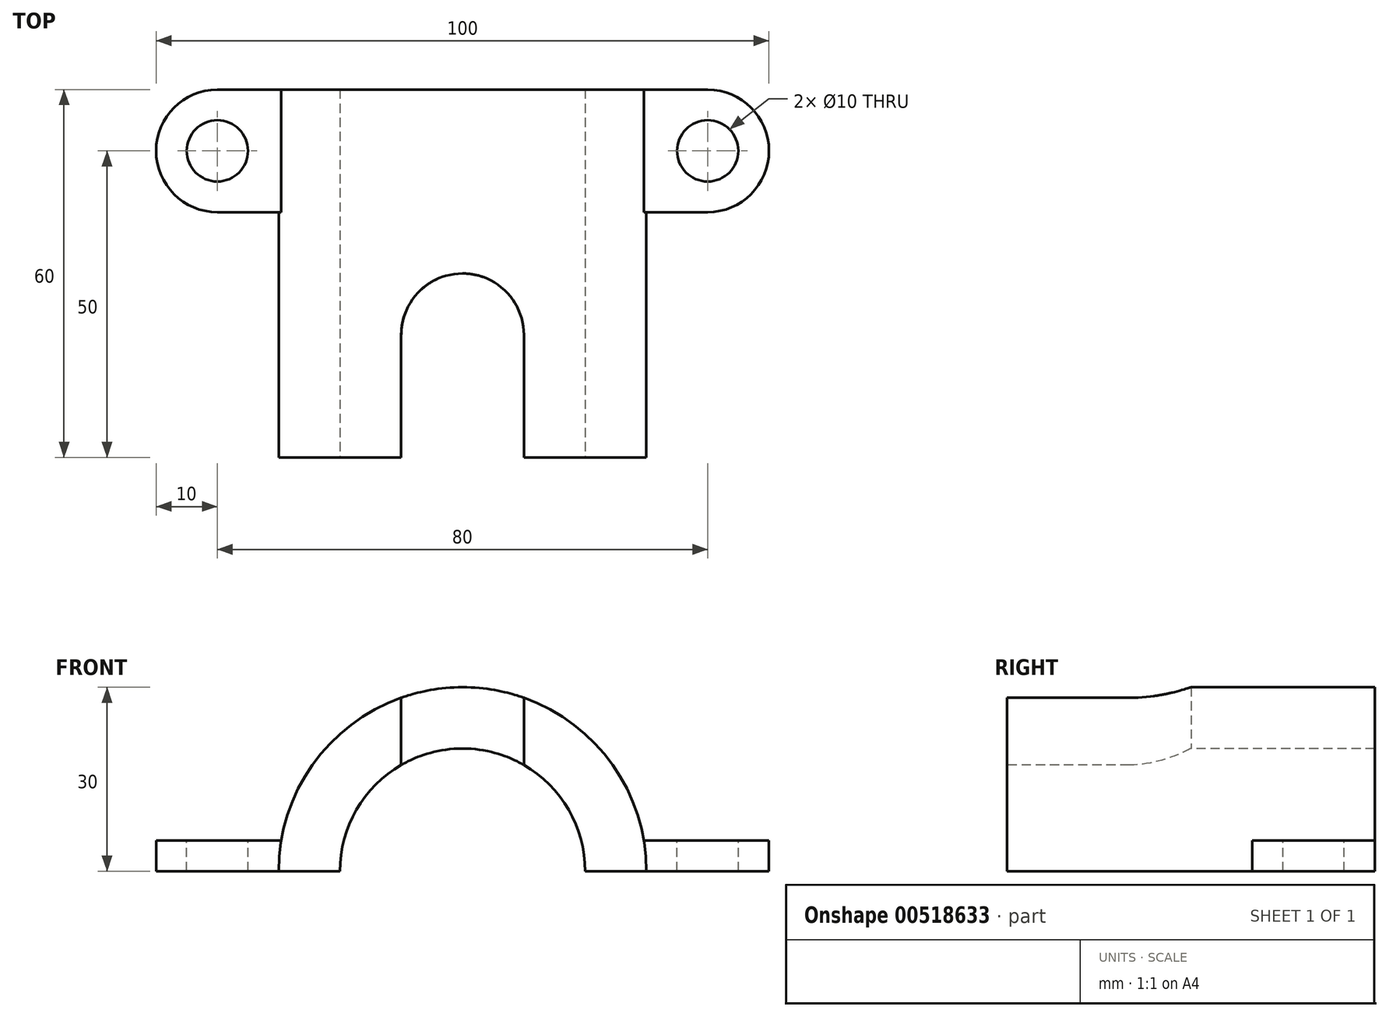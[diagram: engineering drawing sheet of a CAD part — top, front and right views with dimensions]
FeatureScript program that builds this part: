
annotation { "Feature Type Name" : "Feature", "Feature Type Description" : "" }
export const myFeature = defineFeature(function(context is Context, id is Id, definition is map)
    precondition{}
    {
        {
            assignVariable(context, id + "F0", {"name" : "A", "anyValue" : 5});
        }
        {
            var Q0;
            Q0=qCreatedBy(makeId("Top.planeOp"),FACE);
            var sketch = newSketch(context, id + "F1", { "sketchPlane" : qUnion([Q0])});
            skLineSegment(sketch, "E0.bottom", {"start": v(-30, -30) * mm, "end": v(30, -30) * mm});
            skLineSegment(sketch, "E0.top", {"start": v(-30, 30) * mm, "end": v(30, 30) * mm});
            skLineSegment(sketch, "E0.left", {"start": v(-30, -30) * mm, "end": v(-30, 30) * mm});
            skLineSegment(sketch, "E0.right", {"start": v(30, -30) * mm, "end": v(30, 30) * mm});
            skSolve(sketch);
        }
        {
            var Q0;
            Q0=makeQuery(id+"F1.imprint","IMPRINT",FACE,{"disambiguationData":[TD([[makeQuery(id+"F1.imprint","IMPRINT",EDGE,{"derivedFrom":sQuery(id+"F1.wireOp",EDGE,"E0.bottom")}),1.0]])]});
            extrude(context, id + "F2", {"entities" : qUnion([Q0]), "depth" : 30 * mm, "offsetDistance" : 25 * mm});
        }
        {
            var Q0;
            Q0=makeQuery(id+"F2.opExtrude","SWEPT_FACE",FACE,{"disambiguationData":[OSD([sQuery(id+"F1.wireOp",EDGE,"E0.bottom")])]});
            var sketch = newSketch(context, id + "F3", { "sketchPlane" : qUnion([Q0])});
            skLineSegment(sketch, "E1", {"start": v(0, 30) * mm, "end": v(0, 0) * mm});
            skCircle(sketch, "E2", {"center": v(0, 0) * mm, "radius": 30 * mm});
            skCircle(sketch, "E3", {"center": v(0, 0) * mm, "radius": 20 * mm});
            skSolve(sketch);
        }
        {
            var Q0;
            {var subQ0=sQuery(id+"F3.wireOp",EDGE,"E1");var subQ1=makeQuery(id+"F2.opExtrude","CAP_EDGE",EDGE,{"disambiguationData":[OSD([sQuery(id+"F1.wireOp",EDGE,"E0.bottom")])],"isStart":true});var subQ2=makeQuery(id+"F3.imprint","INTERSECT",VERTEX,{"derivedFrom":[subQ1,subQ0]});Q0=makeQuery(id+"F3.imprint","IMPRINT",FACE,{"disambiguationData":[TD([[makeQuery(id+"F3.imprint","IMPRINT",EDGE,{"disambiguationData":[TD([[subQ2,1.0]])],"derivedFrom":subQ0}),1.0]])]});}
            var Q1;
            {var subQ0=sQuery(id+"F3.wireOp",EDGE,"E1");var subQ1=makeQuery(id+"F2.opExtrude","CAP_EDGE",EDGE,{"disambiguationData":[OSD([sQuery(id+"F1.wireOp",EDGE,"E0.bottom")])],"isStart":true});var subQ2=makeQuery(id+"F3.imprint","INTERSECT",VERTEX,{"derivedFrom":[subQ1,subQ0]});Q1=makeQuery(id+"F3.imprint","IMPRINT",FACE,{"disambiguationData":[TD([[makeQuery(id+"F3.imprint","IMPRINT",EDGE,{"disambiguationData":[TD([[subQ2,1.0]])],"derivedFrom":subQ0}),-1.0]])]});}
            extrude(context, id + "F4", {"entities" : qUnion([Q0, Q1]), "operationType" : NewBodyOperationType.REMOVE, "endBound" : BoundingType.THROUGH_ALL, "oppositeDirection" : true, "depth" : 25 * mm, "offsetDistance" : 25 * mm});
        }
        {
            var Q0;
            Q0=qCreatedBy(makeId("Top.planeOp"),FACE);
            var sketch = newSketch(context, id + "F5", { "sketchPlane" : qUnion([Q0])});
            skLineSegment(sketch, "E4.bottom", {"start": v(30, 30) * mm, "end": v(50, 30) * mm});
            skLineSegment(sketch, "E4.top", {"start": v(30, 10) * mm, "end": v(50, 10) * mm});
            skLineSegment(sketch, "E4.left", {"start": v(30, 30) * mm, "end": v(30, -30) * mm});
            skLineSegment(sketch, "E4.right", {"start": v(50, 30) * mm, "end": v(50, 10) * mm});
            skSolve(sketch);
        }
        {
            var Q0;
            Q0=makeQuery(id+"F5.imprint","IMPRINT",FACE,{"disambiguationData":[TD([[makeQuery(id+"F5.imprint","IMPRINT",EDGE,{"derivedFrom":sQuery(id+"F5.wireOp",EDGE,"E4.bottom")}),-1.0]])]});
            extrude(context, id + "F6", {"entities" : qUnion([Q0]), "operationType" : NewBodyOperationType.ADD, "depth" : (getVariable(context, 'A')) * mm, "offsetDistance" : 25 * mm});
        }
        {
            var Q0;
            Q0=qCreatedBy(makeId("Top.planeOp"),FACE);
            var sketch = newSketch(context, id + "F7", { "sketchPlane" : qUnion([Q0])});
            skLineSegment(sketch, "E5.bottom", {"start": v(-30, 10) * mm, "end": v(-50, 10) * mm});
            skLineSegment(sketch, "E5.top", {"start": v(-30, 30) * mm, "end": v(-50, 30) * mm});
            skLineSegment(sketch, "E5.left", {"start": v(-30, 10) * mm, "end": v(-30, 30) * mm});
            skLineSegment(sketch, "E5.right", {"start": v(-50, 10) * mm, "end": v(-50, 30) * mm});
            skSolve(sketch);
        }
        {
            var Q0;
            Q0 = qSketchRegion(id + "F7", true);
            extrude(context, id + "F8", {"entities" : qUnion([Q0]), "operationType" : NewBodyOperationType.ADD, "depth" : (getVariable(context, 'A')) * mm, "offsetDistance" : 25 * mm});
        }
        {
            var Q0;
            Q0=makeQuery(id+"F8.boolean.opBoolean","MERGE",FACE,{"derivedFrom":[makeQuery(id+"F6.boolean.opBoolean","MERGE",FACE,{"derivedFrom":[makeQuery(id+"F2.opExtrude","SWEPT_FACE",FACE,{"disambiguationData":[OSD([sQuery(id+"F1.wireOp",EDGE,"E0.top")])]}),makeQuery(id+"F6.opExtrude","SWEPT_FACE",FACE,{"disambiguationData":[OSD([sQuery(id+"F5.wireOp",EDGE,"E4.bottom")])]})]}),makeQuery(id+"F8.opExtrude","SWEPT_FACE",FACE,{"disambiguationData":[OSD([sQuery(id+"F7.wireOp",EDGE,"E5.top")])]})]});
            var sketch = newSketch(context, id + "F9", { "sketchPlane" : qUnion([Q0])});
            skCircle(sketch, "E6", {"center": v(0, 0) * mm, "radius": 30 * mm});
            skLineSegment(sketch, "E7", {"start": v(-30, 5) * mm, "end": v(-29.58, 5) * mm});
            skLineSegment(sketch, "E8", {"start": v(30, 5) * mm, "end": v(29.58, 5) * mm});
            skSolve(sketch);
        }
        {
            var Q0;
            {var subQ0=sQuery(id+"F9.wireOp",EDGE,"E7");Q0=makeQuery(id+"F9.imprint","IMPRINT",FACE,{"disambiguationData":[TD([[makeQuery(id+"F9.imprint","IMPRINT",EDGE,{"derivedFrom":subQ0}),1.0]])]});}
            var Q1;
            {var subQ0=sQuery(id+"F9.wireOp",EDGE,"E8");Q1=makeQuery(id+"F9.imprint","IMPRINT",FACE,{"disambiguationData":[TD([[makeQuery(id+"F9.imprint","IMPRINT",EDGE,{"derivedFrom":subQ0}),-1.0]])]});}
            extrude(context, id + "F10", {"entities" : qUnion([Q0, Q1]), "operationType" : NewBodyOperationType.REMOVE, "oppositeDirection" : true, "depth" : 20 * mm, "offsetDistance" : 25 * mm});
        }
        {
            var Q0;
            Q0=makeQuery(id+"F2.opExtrude","SWEPT_FACE",FACE,{"disambiguationData":[OSD([sQuery(id+"F1.wireOp",EDGE,"E0.bottom")])]});
            var sketch = newSketch(context, id + "F11", { "sketchPlane" : qUnion([Q0])});
            skCircle(sketch, "E9", {"center": v(0, 0) * mm, "radius": 30 * mm});
            skSolve(sketch);
        }
        {
            var Q0;
            {var subQ1=sQuery(id+"F1.wireOp",EDGE,"E0.bottom");var subQ2=sQuery(id+"F1.wireOp",EDGE,"E0.left");var subQ3=makeQuery(id+"F2.opExtrude","SWEPT_EDGE",EDGE,{"disambiguationData":[OSD([subQ1,subQ2])]});Q0=makeQuery(id+"F11.imprint","IMPRINT",FACE,{"disambiguationData":[TD([[makeQuery(id+"F11.imprint","IMPRINT",EDGE,{"derivedFrom":subQ3}),1.0]])]});}
            var Q1;
            {var subQ1=sQuery(id+"F1.wireOp",EDGE,"E0.bottom");var subQ2=sQuery(id+"F1.wireOp",EDGE,"E0.right");var subQ3=makeQuery(id+"F2.opExtrude","SWEPT_EDGE",EDGE,{"disambiguationData":[OSD([subQ1,subQ2])]});Q1=makeQuery(id+"F11.imprint","IMPRINT",FACE,{"disambiguationData":[TD([[makeQuery(id+"F11.imprint","IMPRINT",EDGE,{"derivedFrom":subQ3}),-1.0]])]});}
            extrude(context, id + "F12", {"entities" : qUnion([Q0, Q1]), "operationType" : NewBodyOperationType.REMOVE, "oppositeDirection" : true, "depth" : 40 * mm, "offsetDistance" : 25 * mm});
        }
        {
            var Q0;
            Q0=makeQuery(id+"F6.opExtrude","SWEPT_EDGE",EDGE,{"disambiguationData":[OSD([sQuery(id+"F5.wireOp",EDGE,"E4.bottom"),sQuery(id+"F5.wireOp",EDGE,"E4.right")])]});
            var Q1;
            Q1=makeQuery(id+"F6.opExtrude","SWEPT_EDGE",EDGE,{"disambiguationData":[OSD([sQuery(id+"F5.wireOp",EDGE,"E4.top"),sQuery(id+"F5.wireOp",EDGE,"E4.right")])]});
            fillet(context, id + "F13", {"entities" : qUnion([Q0, Q1]), "radius" : 10 * mm, "tangentPropagation" : true, "allowEdgeOverflow" : false});
        }
        {
            var Q0;
            Q0=makeQuery(id+"F8.opExtrude","SWEPT_EDGE",EDGE,{"disambiguationData":[OSD([sQuery(id+"F7.wireOp",EDGE,"E5.top"),sQuery(id+"F7.wireOp",EDGE,"E5.right")])]});
            var Q1;
            Q1=makeQuery(id+"F8.opExtrude","SWEPT_EDGE",EDGE,{"disambiguationData":[OSD([sQuery(id+"F7.wireOp",EDGE,"E5.bottom"),sQuery(id+"F7.wireOp",EDGE,"E5.right")])]});
            fillet(context, id + "F14", {"entities" : qUnion([Q0, Q1]), "radius" : 10 * mm, "tangentPropagation" : true, "allowEdgeOverflow" : false});
        }
        {
            var Q0;
            Q0=makeQuery(id+"F10.boolean.opBoolean","MERGE",FACE,{"derivedFrom":[makeQuery(id+"F8.opExtrude","CAP_FACE",FACE,{"disambiguationData":[OSD([sQuery(id+"F7.wireOp",EDGE,"E5.bottom"),sQuery(id+"F7.wireOp",EDGE,"E5.top"),sQuery(id+"F7.wireOp",EDGE,"E5.left"),sQuery(id+"F7.wireOp",EDGE,"E5.right")])],"isStart":false}),makeQuery(id+"F10.opExtrude","SWEPT_FACE",FACE,{"disambiguationData":[OSD([sQuery(id+"F9.wireOp",EDGE,"E8")])]})]});
            var sketch = newSketch(context, id + "F15", { "sketchPlane" : qUnion([Q0])});
            skCircle(sketch, "E10", {"center": v(-40, 20) * mm, "radius": 5 * mm});
            skSolve(sketch);
        }
        {
            var Q0;
            Q0=makeQuery(id+"F15.imprint","IMPRINT",FACE,{"disambiguationData":[TD([[makeQuery(id+"F15.imprint","IMPRINT",EDGE,{"derivedFrom":sQuery(id+"F15.wireOp",EDGE,"E10")}),1.0]])]});
            extrude(context, id + "F16", {"entities" : qUnion([Q0]), "operationType" : NewBodyOperationType.REMOVE, "endBound" : BoundingType.THROUGH_ALL, "oppositeDirection" : true, "depth" : 25 * mm, "offsetDistance" : 25 * mm});
        }
        {
            var Q0;
            Q0=makeQuery(id+"F10.boolean.opBoolean","MERGE",FACE,{"derivedFrom":[makeQuery(id+"F6.opExtrude","CAP_FACE",FACE,{"disambiguationData":[OSD([sQuery(id+"F5.wireOp",EDGE,"E4.bottom"),sQuery(id+"F5.wireOp",EDGE,"E4.top"),sQuery(id+"F5.wireOp",EDGE,"E4.left"),sQuery(id+"F5.wireOp",EDGE,"E4.right")])],"isStart":false}),makeQuery(id+"F10.opExtrude","SWEPT_FACE",FACE,{"disambiguationData":[OSD([sQuery(id+"F9.wireOp",EDGE,"E7")])]})]});
            var sketch = newSketch(context, id + "F17", { "sketchPlane" : qUnion([Q0])});
            skCircle(sketch, "E11", {"center": v(40, 20) * mm, "radius": 5 * mm});
            skSolve(sketch);
        }
        {
            var Q0;
            Q0=makeQuery(id+"F17.imprint","IMPRINT",FACE,{"disambiguationData":[TD([[makeQuery(id+"F17.imprint","IMPRINT",EDGE,{"derivedFrom":sQuery(id+"F17.wireOp",EDGE,"E11")}),1.0]])]});
            extrude(context, id + "F18", {"entities" : qUnion([Q0]), "operationType" : NewBodyOperationType.REMOVE, "endBound" : BoundingType.THROUGH_ALL, "oppositeDirection" : true, "depth" : 25 * mm, "offsetDistance" : 25 * mm});
        }
        {
            var Q0;
            Q0=makeQuery(id+"F2.opExtrude","SWEPT_FACE",FACE,{"disambiguationData":[OSD([sQuery(id+"F1.wireOp",EDGE,"E0.bottom")])]});
            var sketch = newSketch(context, id + "F19", { "sketchPlane" : qUnion([Q0])});
            skLineSegment(sketch, "E12", {"start": v(10, 28.28) * mm, "end": v(10, 17.32) * mm});
            skLineSegment(sketch, "E13", {"start": v(-10, 28.28) * mm, "end": v(-10, 17.32) * mm});
            skSolve(sketch);
        }
        {
            var Q0;
            {var subQ0=sQuery(id+"F19.wireOp",EDGE,"E12");Q0=makeQuery(id+"F19.imprint","IMPRINT",FACE,{"disambiguationData":[TD([[makeQuery(id+"F19.imprint","IMPRINT",EDGE,{"derivedFrom":subQ0}),-1.0]])]});}
            extrude(context, id + "F20", {"entities" : qUnion([Q0]), "operationType" : NewBodyOperationType.REMOVE, "oppositeDirection" : true, "depth" : 30 * mm, "offsetDistance" : 25 * mm});
        }
        {
            var Q0;
            Q0=makeQuery(id+"F20.boolean.opBoolean","COPY",EDGE,{"derivedFrom":makeQuery(id+"F20.opExtrude","CAP_EDGE",EDGE,{"disambiguationData":[OSD([sQuery(id+"F19.wireOp",EDGE,"E13")])],"isStart":false})});
            fillet(context, id + "F21", {"entities" : qUnion([Q0]), "radius" : 10 * mm, "tangentPropagation" : true, "allowEdgeOverflow" : false});
        }
        {
            var Q0;
            Q0=makeQuery(id+"F20.boolean.opBoolean","COPY",EDGE,{"derivedFrom":makeQuery(id+"F20.opExtrude","CAP_EDGE",EDGE,{"disambiguationData":[OSD([sQuery(id+"F19.wireOp",EDGE,"E12")])],"isStart":false})});
            fillet(context, id + "F22", {"entities" : qUnion([Q0]), "radius" : 10 * mm, "tangentPropagation" : true, "allowEdgeOverflow" : false});
        }
    });
